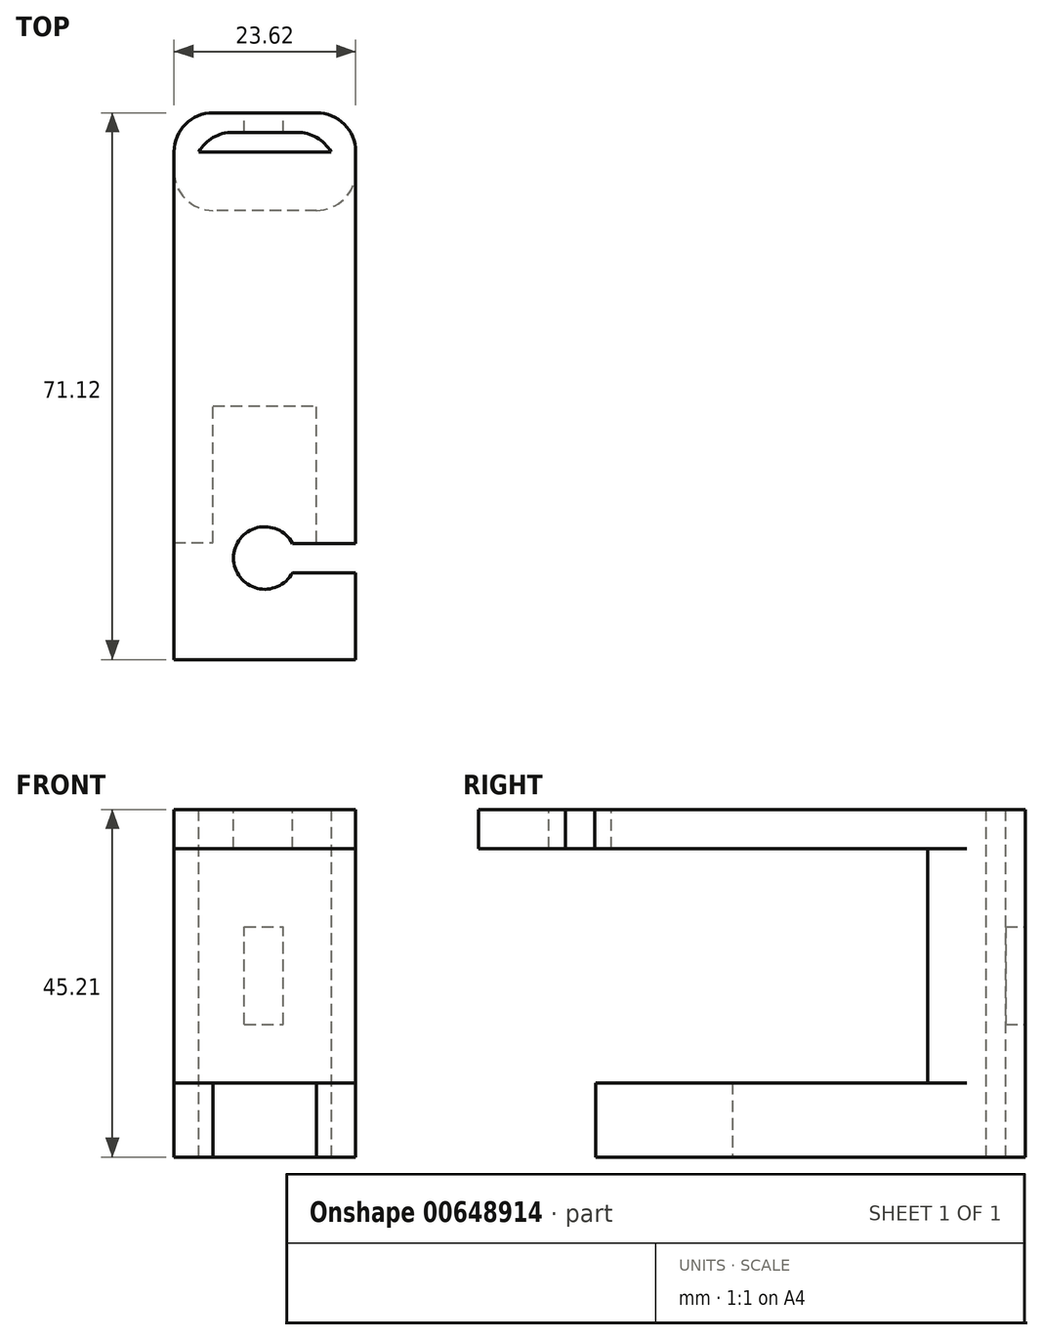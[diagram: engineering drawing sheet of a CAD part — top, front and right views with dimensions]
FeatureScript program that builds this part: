
annotation { "Feature Type Name" : "Feature", "Feature Type Description" : "" }
export const myFeature = defineFeature(function(context is Context, id is Id, definition is map)
    precondition{}
    {
        {
            var Q0;
            Q0=qCreatedBy(makeId("Top.planeOp"),FACE);
            var sketch = newSketch(context, id + "F0", { "sketchPlane" : qUnion([Q0])});
            skLineSegment(sketch, "E0.bottom", {"start": v(-9.27, 0) * mm, "end": v(9.27, 0) * mm});
            skLineSegment(sketch, "E0.top", {"start": v(-9.27, 43.18) * mm, "end": v(9.27, 43.18) * mm});
            skLineSegment(sketch, "E0.left", {"start": v(-9.27, 0) * mm, "end": v(-9.27, 43.18) * mm});
            skLineSegment(sketch, "E0.right", {"start": v(9.27, 0) * mm, "end": v(9.27, 43.18) * mm});
            skLineSegment(sketch, "E1.bottom", {"start": v(-6.73, 0) * mm, "end": v(6.73, 0) * mm});
            skLineSegment(sketch, "E1.top", {"start": v(-6.73, 12.7) * mm, "end": v(6.73, 12.7) * mm});
            skLineSegment(sketch, "E1.left", {"start": v(-6.73, 0) * mm, "end": v(-6.73, 12.7) * mm});
            skLineSegment(sketch, "E1.right", {"start": v(6.73, 0) * mm, "end": v(6.73, 12.7) * mm});
            skSolve(sketch);
        }
        {
            var Q0;
            Q0=makeQuery(id+"F0.imprint","IMPRINT",FACE,{"disambiguationData":[TD([[makeQuery(id+"F0.imprint","IMPRINT",EDGE,{"derivedFrom":sQuery(id+"F0.wireOp",EDGE,"E0.top")}),-1.0]])]});
            extrude(context, id + "F1", {"entities" : qUnion([Q0]), "depth" : 5.84 * mm, "offsetDistance" : 25.4 * mm});
        }
        {
            var Q0;
            Q0=makeQuery(id+"F1.opExtrude","SWEPT_FACE",FACE,{"disambiguationData":[OSD([sQuery(id+"F0.wireOp",EDGE,"E0.top")])]});
            extrude(context, id + "F2", {"entities" : qUnion([Q0]), "operationType" : NewBodyOperationType.ADD, "depth" : 5.08 * mm, "offsetDistance" : 25.4 * mm});
        }
        {
            var Q0;
            {var subQ0=sQuery(id+"F0.wireOp",EDGE,"E0.top");Q0=makeQuery(id+"F2.boolean.opBoolean","MERGE",FACE,{"derivedFrom":[makeQuery(id+"F1.opExtrude","CAP_FACE",FACE,{"disambiguationData":[OSD([sQuery(id+"F0.wireOp",EDGE,"E0.bottom"),subQ0,sQuery(id+"F0.wireOp",EDGE,"E0.left"),sQuery(id+"F0.wireOp",EDGE,"E0.right"),sQuery(id+"F0.wireOp",EDGE,"E1.top"),sQuery(id+"F0.wireOp",EDGE,"E1.left"),sQuery(id+"F0.wireOp",EDGE,"E1.right")])],"isStart":false}),makeQuery(id+"F2.opExtrude","SWEPT_FACE",FACE,{"disambiguationData":[OSD([subQ0]),TDD([makeQuery(id+"F1.opExtrude","CAP_EDGE",EDGE,{"disambiguationData":[OSD([subQ0])],"isStart":false})])]})]});}
            var sketch = newSketch(context, id + "F3", { "sketchPlane" : qUnion([Q0])});
            skLineSegment(sketch, "E2.bottom", {"start": v(9.27, 48.26) * mm, "end": v(-9.27, 48.26) * mm});
            skLineSegment(sketch, "E2.top", {"start": v(9.27, 43.18) * mm, "end": v(-9.27, 43.18) * mm});
            skLineSegment(sketch, "E2.left", {"start": v(9.27, 48.26) * mm, "end": v(9.27, 43.18) * mm});
            skLineSegment(sketch, "E2.right", {"start": v(-9.27, 48.26) * mm, "end": v(-9.27, 43.18) * mm});
            skSolve(sketch);
        }
        {
            var Q0;
            Q0=makeQuery(id+"F3.imprint","IMPRINT",FACE,{"disambiguationData":[TD([[makeQuery(id+"F3.imprint","IMPRINT",EDGE,{"derivedFrom":sQuery(id+"F3.wireOp",EDGE,"E2.bottom")}),-1.0]])]});
            extrude(context, id + "F4", {"entities" : qUnion([Q0]), "operationType" : NewBodyOperationType.ADD, "depth" : 35.56 * mm, "offsetDistance" : 25.4 * mm});
        }
        {
            var Q0;
            Q0=makeQuery(id+"F4.opExtrude","SWEPT_FACE",FACE,{"disambiguationData":[OSD([sQuery(id+"F3.wireOp",EDGE,"E2.top")])]});
            var sketch = newSketch(context, id + "F5", { "sketchPlane" : qUnion([Q0])});
            skLineSegment(sketch, "E3.bottom", {"start": v(-9.27, 41.4) * mm, "end": v(9.27, 41.4) * mm});
            skLineSegment(sketch, "E3.top", {"start": v(-9.27, 36.32) * mm, "end": v(9.27, 36.32) * mm});
            skLineSegment(sketch, "E3.left", {"start": v(-9.27, 41.4) * mm, "end": v(-9.27, 36.32) * mm});
            skLineSegment(sketch, "E3.right", {"start": v(9.27, 41.4) * mm, "end": v(9.27, 36.32) * mm});
            skSolve(sketch);
        }
        {
            var Q0;
            Q0=makeQuery(id+"F5.imprint","IMPRINT",FACE,{"disambiguationData":[TD([[makeQuery(id+"F5.imprint","IMPRINT",EDGE,{"derivedFrom":sQuery(id+"F5.wireOp",EDGE,"E3.bottom")}),1.0]])]});
            extrude(context, id + "F6", {"entities" : qUnion([Q0]), "operationType" : NewBodyOperationType.ADD, "depth" : 58.42 * mm, "offsetDistance" : 25.4 * mm});
        }
        {
            var Q0;
            Q0=makeQuery(id+"F6.boolean.opBoolean","MERGE",FACE,{"derivedFrom":[makeQuery(id+"F4.opExtrude","CAP_FACE",FACE,{"disambiguationData":[OSD([sQuery(id+"F3.wireOp",EDGE,"E2.bottom"),sQuery(id+"F3.wireOp",EDGE,"E2.top"),sQuery(id+"F3.wireOp",EDGE,"E2.left"),sQuery(id+"F3.wireOp",EDGE,"E2.right")])],"isStart":false}),makeQuery(id+"F6.opExtrude","SWEPT_FACE",FACE,{"disambiguationData":[OSD([sQuery(id+"F5.wireOp",EDGE,"E3.bottom")])]})]});
            var sketch = newSketch(context, id + "F7", { "sketchPlane" : qUnion([Q0])});
            skCircle(sketch, "E4", {"center": v(0, -2.03) * mm, "radius": 4.06 * mm});
            skLineSegment(sketch, "E5.bottom", {"start": v(3.59, -3.94) * mm, "end": v(28.99, -3.94) * mm});
            skLineSegment(sketch, "E5.top", {"start": v(3.59, -0.13) * mm, "end": v(28.99, -0.13) * mm});
            skLineSegment(sketch, "E5.left", {"start": v(3.59, -3.94) * mm, "end": v(3.59, -0.13) * mm});
            skLineSegment(sketch, "E5.right", {"start": v(28.99, -3.94) * mm, "end": v(28.99, -0.13) * mm});
            skSolve(sketch);
        }
        {
            var Q0;
            {var subQ0=sQuery(id+"F0.wireOp",EDGE,"E0.left");Q0=makeQuery(id+"F6.boolean.opBoolean","MERGE",FACE,{"derivedFrom":[makeQuery(id+"F4.boolean.opBoolean","MERGE",FACE,{"derivedFrom":[makeQuery(id+"F2.boolean.opBoolean","MERGE",FACE,{"derivedFrom":[makeQuery(id+"F1.opExtrude","SWEPT_FACE",FACE,{"disambiguationData":[OSD([subQ0])]}),makeQuery(id+"F2.opExtrude","SWEPT_FACE",FACE,{"disambiguationData":[OSD([sQuery(id+"F0.wireOp",EDGE,"E0.top"),subQ0])]})]}),makeQuery(id+"F4.opExtrude","SWEPT_FACE",FACE,{"disambiguationData":[OSD([sQuery(id+"F3.wireOp",EDGE,"E2.right")])]})]}),makeQuery(id+"F6.opExtrude","SWEPT_FACE",FACE,{"disambiguationData":[OSD([sQuery(id+"F5.wireOp",EDGE,"E3.left")])]})]});}
            extrude(context, id + "F8", {"entities" : qUnion([Q0]), "operationType" : NewBodyOperationType.ADD, "depth" : 2.54 * mm, "offsetDistance" : 25.4 * mm});
        }
        {
            var Q0;
            {var subQ0=sQuery(id+"F0.wireOp",EDGE,"E0.right");Q0=makeQuery(id+"F6.boolean.opBoolean","MERGE",FACE,{"derivedFrom":[makeQuery(id+"F4.boolean.opBoolean","MERGE",FACE,{"derivedFrom":[makeQuery(id+"F2.boolean.opBoolean","MERGE",FACE,{"derivedFrom":[makeQuery(id+"F1.opExtrude","SWEPT_FACE",FACE,{"disambiguationData":[OSD([subQ0])]}),makeQuery(id+"F2.opExtrude","SWEPT_FACE",FACE,{"disambiguationData":[OSD([sQuery(id+"F0.wireOp",EDGE,"E0.top"),subQ0])]})]}),makeQuery(id+"F4.opExtrude","SWEPT_FACE",FACE,{"disambiguationData":[OSD([sQuery(id+"F3.wireOp",EDGE,"E2.left")])]})]}),makeQuery(id+"F6.opExtrude","SWEPT_FACE",FACE,{"disambiguationData":[OSD([sQuery(id+"F5.wireOp",EDGE,"E3.right")])]})]});}
            extrude(context, id + "F9", {"entities" : qUnion([Q0]), "operationType" : NewBodyOperationType.ADD, "depth" : 2.54 * mm, "offsetDistance" : 25.4 * mm});
        }
        {
            var Q0;
            {var subQ0=sQuery(id+"F7.wireOp",EDGE,"E5.left");var subQ1=sQuery(id+"F7.wireOp",EDGE,"E5.bottom");var subQ2=sQuery(id+"F7.wireOp",EDGE,"E4");var subQ3=makeQuery(id+"F7.imprint","INTERSECT",VERTEX,{"derivedFrom":[subQ2,subQ1,subQ0]});Q0=makeQuery(id+"F7.imprint","IMPRINT",FACE,{"disambiguationData":[TD([[makeQuery(id+"F7.imprint","IMPRINT",EDGE,{"disambiguationData":[TD([[subQ3,-1.0]])],"derivedFrom":subQ2}),-1.0]])]});}
            var Q1;
            {var subQ0=sQuery(id+"F7.wireOp",EDGE,"E5.left");Q1=makeQuery(id+"F7.imprint","IMPRINT",FACE,{"disambiguationData":[TD([[makeQuery(id+"F7.imprint","IMPRINT",EDGE,{"derivedFrom":subQ0}),1.0]])]});}
            var Q2;
            {var subQ0=sQuery(id+"F7.wireOp",EDGE,"E5.left");Q2=makeQuery(id+"F7.imprint","IMPRINT",FACE,{"disambiguationData":[TD([[makeQuery(id+"F7.imprint","IMPRINT",EDGE,{"derivedFrom":subQ0}),-1.0]])]});}
            var Q3;
            {var subQ0=sQuery(id+"F7.wireOp",EDGE,"E5.right");Q3=makeQuery(id+"F7.imprint","IMPRINT",FACE,{"disambiguationData":[TD([[makeQuery(id+"F7.imprint","IMPRINT",EDGE,{"derivedFrom":subQ0}),1.0]])]});}
            extrude(context, id + "F10", {"entities" : qUnion([Q0, Q1, Q2, Q3]), "operationType" : NewBodyOperationType.REMOVE, "oppositeDirection" : true, "depth" : 25.4 * mm, "offsetDistance" : 25.4 * mm});
        }
        {
            var Q0;
            {var subQ0=sQuery(id+"F0.wireOp",EDGE,"E0.right");var subQ1=sQuery(id+"F0.wireOp",EDGE,"E0.top");var subQ2=sQuery(id+"F0.wireOp",EDGE,"E0.left");Q0=makeQuery(id+"F9.boolean.opBoolean","MERGE",FACE,{"derivedFrom":[makeQuery(id+"F8.boolean.opBoolean","MERGE",FACE,{"derivedFrom":[makeQuery(id+"F2.boolean.opBoolean","MERGE",FACE,{"derivedFrom":[makeQuery(id+"F1.opExtrude","CAP_FACE",FACE,{"disambiguationData":[OSD([sQuery(id+"F0.wireOp",EDGE,"E0.bottom"),subQ1,subQ2,subQ0,sQuery(id+"F0.wireOp",EDGE,"E1.top"),sQuery(id+"F0.wireOp",EDGE,"E1.left"),sQuery(id+"F0.wireOp",EDGE,"E1.right")])],"isStart":true}),makeQuery(id+"F2.opExtrude","SWEPT_FACE",FACE,{"disambiguationData":[OSD([subQ1]),TDD([makeQuery(id+"F1.opExtrude","CAP_EDGE",EDGE,{"disambiguationData":[OSD([subQ1])],"isStart":true})])]})]}),makeQuery(id+"F8.opExtrude","SWEPT_FACE",FACE,{"disambiguationData":[OSD([subQ1,subQ2]),TDD([makeQuery(id+"F2.boolean.opBoolean","MERGE",EDGE,{"derivedFrom":[makeQuery(id+"F1.opExtrude","CAP_EDGE",EDGE,{"disambiguationData":[OSD([subQ2])],"isStart":true}),makeQuery(id+"F2.opExtrude","SWEPT_EDGE",EDGE,{"disambiguationData":[OSD([subQ1,subQ2]),TDD([makeQuery(id+"F1.opExtrude","CAP_VERTEX",VERTEX,{"disambiguationData":[OSD([subQ1,subQ2])],"isStart":true})])]})]})])]})]}),makeQuery(id+"F9.opExtrude","SWEPT_FACE",FACE,{"disambiguationData":[OSD([subQ1,subQ0]),TDD([makeQuery(id+"F2.boolean.opBoolean","MERGE",EDGE,{"derivedFrom":[makeQuery(id+"F1.opExtrude","CAP_EDGE",EDGE,{"disambiguationData":[OSD([subQ0])],"isStart":true}),makeQuery(id+"F2.opExtrude","SWEPT_EDGE",EDGE,{"disambiguationData":[OSD([subQ1,subQ0]),TDD([makeQuery(id+"F1.opExtrude","CAP_VERTEX",VERTEX,{"disambiguationData":[OSD([subQ1,subQ0])],"isStart":true})])]})]})])]})]});}
            extrude(context, id + "F11", {"entities" : qUnion([Q0]), "operationType" : NewBodyOperationType.ADD, "depth" : 3.8 * mm, "offsetDistance" : 25.4 * mm});
        }
        {
            var Q0;
            {var subQ0=sQuery(id+"F0.wireOp",EDGE,"E1.top");Q0=makeQuery(id+"F11.boolean.opBoolean","MERGE",FACE,{"derivedFrom":[makeQuery(id+"F1.opExtrude","SWEPT_FACE",FACE,{"disambiguationData":[OSD([subQ0])]}),makeQuery(id+"F11.opExtrude","SWEPT_FACE",FACE,{"disambiguationData":[OSD([subQ0])]})]});}
            extrude(context, id + "F12", {"entities" : qUnion([Q0]), "operationType" : NewBodyOperationType.REMOVE, "oppositeDirection" : true, "depth" : 5.08 * mm, "offsetDistance" : 25.4 * mm});
        }
        {
            var Q0;
            {var subQ0=sQuery(id+"F0.wireOp",EDGE,"E0.right");var subQ1=sQuery(id+"F0.wireOp",EDGE,"E0.left");var subQ2=sQuery(id+"F0.wireOp",EDGE,"E0.top");var subQ3=sQuery(id+"F3.wireOp",EDGE,"E2.bottom");Q0=makeQuery(id+"F11.boolean.opBoolean","MERGE",FACE,{"derivedFrom":[makeQuery(id+"F9.boolean.opBoolean","MERGE",FACE,{"derivedFrom":[makeQuery(id+"F8.boolean.opBoolean","MERGE",FACE,{"derivedFrom":[makeQuery(id+"F4.boolean.opBoolean","MERGE",FACE,{"derivedFrom":[makeQuery(id+"F2.opExtrude","CAP_FACE",FACE,{"disambiguationData":[OSD([subQ2])],"isStart":false}),makeQuery(id+"F4.opExtrude","SWEPT_FACE",FACE,{"disambiguationData":[OSD([subQ3])]})]}),makeQuery(id+"F8.opExtrude","SWEPT_FACE",FACE,{"disambiguationData":[OSD([subQ2,subQ1,subQ3,sQuery(id+"F3.wireOp",EDGE,"E2.right")])]})]}),makeQuery(id+"F9.opExtrude","SWEPT_FACE",FACE,{"disambiguationData":[OSD([subQ2,subQ0,subQ3,sQuery(id+"F3.wireOp",EDGE,"E2.left")])]})]}),makeQuery(id+"F11.opExtrude","SWEPT_FACE",FACE,{"disambiguationData":[OSD([subQ2,subQ1,subQ0])]})]});}
            extrude(context, id + "F13", {"entities" : qUnion([Q0]), "operationType" : NewBodyOperationType.ADD, "depth" : 7.62 * mm, "offsetDistance" : 25.4 * mm});
        }
        {
            var Q0;
            {var subQ0=sQuery(id+"F3.wireOp",EDGE,"E2.right");var subQ1=sQuery(id+"F3.wireOp",EDGE,"E2.left");var subQ2=sQuery(id+"F3.wireOp",EDGE,"E2.bottom");var subQ3=sQuery(id+"F5.wireOp",EDGE,"E3.bottom");Q0=makeQuery(id+"F13.boolean.opBoolean","MERGE",FACE,{"derivedFrom":[makeQuery(id+"F9.boolean.opBoolean","MERGE",FACE,{"derivedFrom":[makeQuery(id+"F8.boolean.opBoolean","MERGE",FACE,{"derivedFrom":[makeQuery(id+"F6.boolean.opBoolean","MERGE",FACE,{"derivedFrom":[makeQuery(id+"F4.opExtrude","CAP_FACE",FACE,{"disambiguationData":[OSD([subQ2,sQuery(id+"F3.wireOp",EDGE,"E2.top"),subQ1,subQ0])],"isStart":false}),makeQuery(id+"F6.opExtrude","SWEPT_FACE",FACE,{"disambiguationData":[OSD([subQ3])]})]}),makeQuery(id+"F8.opExtrude","SWEPT_FACE",FACE,{"disambiguationData":[OSD([subQ0,subQ3,sQuery(id+"F5.wireOp",EDGE,"E3.left")])]})]}),makeQuery(id+"F9.opExtrude","SWEPT_FACE",FACE,{"disambiguationData":[OSD([subQ1,subQ3,sQuery(id+"F5.wireOp",EDGE,"E3.right")])]})]}),makeQuery(id+"F13.opExtrude","SWEPT_FACE",FACE,{"disambiguationData":[OSD([subQ2,subQ1,subQ0])]})]});}
            var sketch = newSketch(context, id + "F14", { "sketchPlane" : qUnion([Q0])});
            skLineSegment(sketch, "E6.bottom", {"start": v(-9.27, 53.34) * mm, "end": v(9.27, 53.34) * mm});
            skLineSegment(sketch, "E6.top", {"start": v(-9.27, 48.26) * mm, "end": v(9.27, 48.26) * mm});
            skLineSegment(sketch, "E6.left", {"start": v(-9.27, 53.34) * mm, "end": v(-9.27, 48.26) * mm});
            skLineSegment(sketch, "E6.right", {"start": v(9.27, 53.34) * mm, "end": v(9.27, 48.26) * mm});
            skSolve(sketch);
        }
        {
            var Q0;
            Q0=makeQuery(id+"F14.imprint","IMPRINT",FACE,{"disambiguationData":[TD([[makeQuery(id+"F14.imprint","IMPRINT",EDGE,{"derivedFrom":sQuery(id+"F14.wireOp",EDGE,"E6.bottom")}),-1.0]])]});
            extrude(context, id + "F15", {"entities" : qUnion([Q0]), "operationType" : NewBodyOperationType.REMOVE, "oppositeDirection" : true, "depth" : 127 * mm, "offsetDistance" : 25.4 * mm});
        }
        {
            var Q0;
            Q0=makeQuery(id+"F13.opExtrude","CAP_EDGE",EDGE,{"disambiguationData":[OSD([sQuery(id+"F0.wireOp",EDGE,"E0.top"),sQuery(id+"F0.wireOp",EDGE,"E0.right"),sQuery(id+"F3.wireOp",EDGE,"E2.bottom"),sQuery(id+"F3.wireOp",EDGE,"E2.left")])],"isStart":false});
            var Q1;
            Q1=makeQuery(id+"F13.opExtrude","CAP_EDGE",EDGE,{"disambiguationData":[OSD([sQuery(id+"F0.wireOp",EDGE,"E0.top"),sQuery(id+"F0.wireOp",EDGE,"E0.left"),sQuery(id+"F3.wireOp",EDGE,"E2.bottom"),sQuery(id+"F3.wireOp",EDGE,"E2.right")])],"isStart":false});
            var Q2;
            Q2=makeQuery(id+"F15.boolean.opBoolean","COPY",EDGE,{"derivedFrom":makeQuery(id+"F15.opExtrude","SWEPT_EDGE",EDGE,{"disambiguationData":[OSD([sQuery(id+"F14.wireOp",EDGE,"E6.bottom"),sQuery(id+"F14.wireOp",EDGE,"E6.right")])]})});
            var Q3;
            Q3=makeQuery(id+"F15.boolean.opBoolean","COPY",EDGE,{"derivedFrom":makeQuery(id+"F15.opExtrude","SWEPT_EDGE",EDGE,{"disambiguationData":[OSD([sQuery(id+"F14.wireOp",EDGE,"E6.bottom"),sQuery(id+"F14.wireOp",EDGE,"E6.left")])]})});
            fillet(context, id + "F16", {"entities" : qUnion([Q0, Q1, Q2, Q3]), "radius" : 5.08 * mm, "tangentPropagation" : true, "allowEdgeOverflow" : false});
        }
        {
            var Q0;
            Q0=makeQuery(id+"F8.opExtrude","CAP_EDGE",EDGE,{"disambiguationData":[OSD([sQuery(id+"F0.wireOp",EDGE,"E0.top"),sQuery(id+"F0.wireOp",EDGE,"E0.left"),sQuery(id+"F3.wireOp",EDGE,"E2.top"),sQuery(id+"F3.wireOp",EDGE,"E2.right")])],"isStart":false});
            var Q1;
            Q1=makeQuery(id+"F9.opExtrude","CAP_EDGE",EDGE,{"disambiguationData":[OSD([sQuery(id+"F0.wireOp",EDGE,"E0.top"),sQuery(id+"F0.wireOp",EDGE,"E0.right"),sQuery(id+"F3.wireOp",EDGE,"E2.top"),sQuery(id+"F3.wireOp",EDGE,"E2.left")])],"isStart":false});
            fillet(context, id + "F17", {"entities" : qUnion([Q0, Q1]), "radius" : 5.08 * mm, "tangentPropagation" : true, "allowEdgeOverflow" : false});
        }
        {
            var Q0;
            Q0=makeQuery(id+"F15.boolean.opBoolean","COPY",FACE,{"derivedFrom":makeQuery(id+"F15.opExtrude","SWEPT_FACE",FACE,{"disambiguationData":[OSD([sQuery(id+"F14.wireOp",EDGE,"E6.top")])]})});
            extrude(context, id + "F18", {"entities" : qUnion([Q0]), "operationType" : NewBodyOperationType.ADD, "depth" : 2.54 * mm, "offsetDistance" : 25.4 * mm});
        }
        {
            var Q0;
            Q0=makeQuery(id+"F13.opExtrude","CAP_FACE",FACE,{"disambiguationData":[OSD([sQuery(id+"F0.wireOp",EDGE,"E0.top"),sQuery(id+"F0.wireOp",EDGE,"E0.left"),sQuery(id+"F0.wireOp",EDGE,"E0.right"),sQuery(id+"F3.wireOp",EDGE,"E2.bottom"),sQuery(id+"F3.wireOp",EDGE,"E2.left"),sQuery(id+"F3.wireOp",EDGE,"E2.right")])],"isStart":false});
            var sketch = newSketch(context, id + "F19", { "sketchPlane" : qUnion([Q0])});
            skLineSegment(sketch, "E7.bottom", {"start": v(2.67, 13.46) * mm, "end": v(-2.41, 13.46) * mm});
            skLineSegment(sketch, "E7.top", {"start": v(2.67, 26.16) * mm, "end": v(-2.41, 26.16) * mm});
            skLineSegment(sketch, "E7.left", {"start": v(2.67, 13.46) * mm, "end": v(2.67, 26.16) * mm});
            skLineSegment(sketch, "E7.right", {"start": v(-2.41, 13.46) * mm, "end": v(-2.41, 26.16) * mm});
            skSolve(sketch);
        }
        {
            var Q0;
            Q0=makeQuery(id+"F19.imprint","IMPRINT",FACE,{"disambiguationData":[TD([[makeQuery(id+"F19.imprint","IMPRINT",EDGE,{"derivedFrom":sQuery(id+"F19.wireOp",EDGE,"E7.bottom")}),-1.0]])]});
            extrude(context, id + "F20", {"entities" : qUnion([Q0]), "operationType" : NewBodyOperationType.REMOVE, "oppositeDirection" : true, "depth" : 5.08 * mm, "offsetDistance" : 25.4 * mm});
        }
    });
